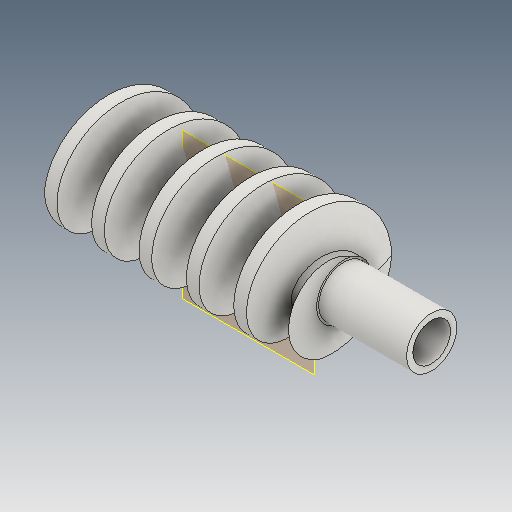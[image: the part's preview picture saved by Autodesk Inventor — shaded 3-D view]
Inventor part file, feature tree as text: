
AUTODESK INVENTOR PART (.ipt)
format: ipt  version: 2020.3 (Build 243373010, 373A)  size: 322,560 bytes
history: native  units: mm (DEFAULTED — no unit token found)
features: other x6, extrude x2, chamfer x2, pattern_circular x2, sketch x2
ambient origin geometry x6: Origin, XZ Plane, X Axis, Y Axis, Z Axis, Center Point
bodies: Solid1 (feature_tree)
feature tree (14):
  extrude  "Base Body"  Depth=48.0mm
  chamfer  "Chamfer1"  [1 undecoded]
  chamfer  "Chamfer2"  Distance=4.804407mm
  other  "Tooth Sketch"
  other  "Tooth"
  pattern_circular  "Tooth Pattern"  [2 undecoded]
  other  "Left Tooth"
  pattern_circular  "Left Tooth Pattern"  [2 undecoded]
  extrude  "Extrusion2"  Depth=35.0mm
  other  "Base Body Sketch"
  sketch  "Sketch5"  dims[d4=40.0mm d5=48.0mm]
  other  "Srf1"
  sketch  "Sketch8"  dims[d6=100.0mm d7=0.0mm d8=4.804407mm d9=13.2mm d10=4.804407mm d11=13.2mm d12=19.198622mm d14=3.1425mm d24=19.198622mm d25=65.973446mm d26=4.712389mm d27=10.8mm d28=18.0mm d29=24.24mm d30=18.849556mm d31=10.0mm d32=80.0mm d33=0.0mm d34=90.0deg d35=90.0deg d36=0.0mm d37=0.0mm d44=10.0mm d46=360.0deg d47=45.0deg d48=45.0deg d49=138.0mm d50=0.0mm d54=0.0mm d56=0.0mm d59=36.0mm d60=10.0mm d61=0.0mm d62=18.849556mm d63=10.0mm d64=80.0mm d65=0.0mm d66=90.0deg d67=90.0deg d68=0.0mm d69=0.0mm d70=10.0mm d71=10.0mm d72=10.0mm d73=360.0deg d75=10.0mm d76=10.0mm d77=0.0mm d79=138.0mm d80=0.0mm d81=20.0mm d82=35.0mm d83=0.0mm d84=15.0mm]
  other  "Pitch Diameter"
note: 5 required parameter values undecoded (feature->parameter linkage not recoverable at this tier; creation-order binding heuristic only, values carry confidence <= 0.55)
